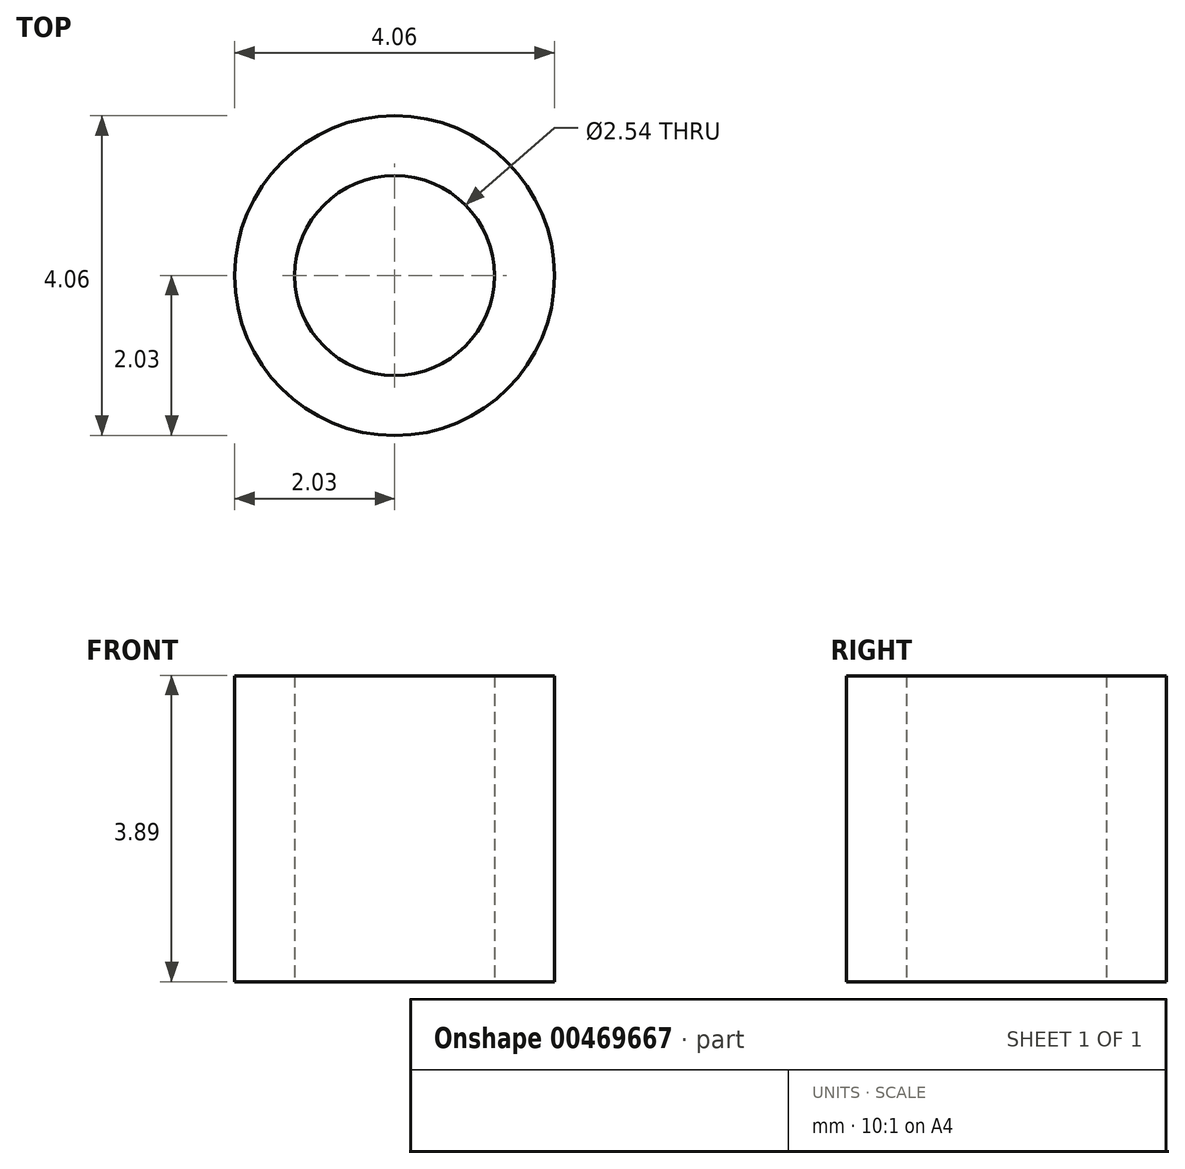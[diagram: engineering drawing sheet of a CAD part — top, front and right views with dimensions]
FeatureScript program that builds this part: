
annotation { "Feature Type Name" : "Feature", "Feature Type Description" : "" }
export const myFeature = defineFeature(function(context is Context, id is Id, definition is map)
    precondition{}
    {
        {
            var Q0;
            Q0=qCreatedBy(makeId("Top.planeOp"),FACE);
            var sketch = newSketch(context, id + "F0", { "sketchPlane" : qUnion([Q0])});
            skCircle(sketch, "E0", {"center": v(0, 0) * mm, "radius": 1.27 * mm});
            skCircle(sketch, "E1", {"center": v(0, 0) * mm, "radius": 2.03 * mm});
            skSolve(sketch);
        }
        {
            var Q0;
            Q0 = qSketchRegion(id + "F0", true);
            extrude(context, id + "F1", {"entities" : qUnion([Q0]), "depth" : 3.9 * mm});
        }
    });
